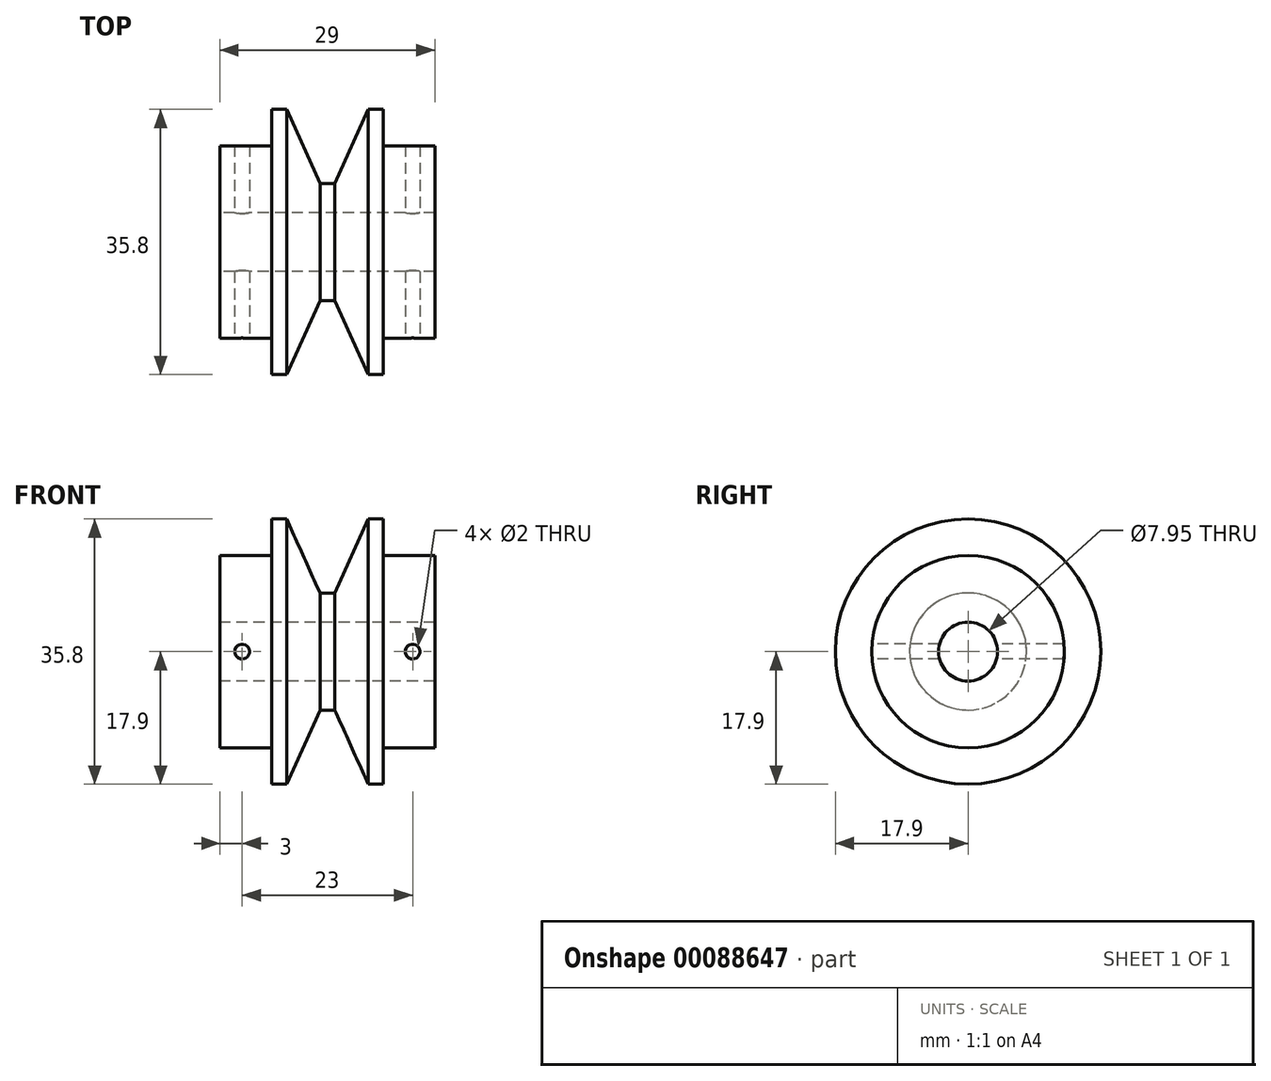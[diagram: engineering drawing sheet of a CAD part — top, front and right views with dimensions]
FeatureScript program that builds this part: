
annotation { "Feature Type Name" : "Feature", "Feature Type Description" : "" }
export const myFeature = defineFeature(function(context is Context, id is Id, definition is map)
    precondition{}
    {
        {
            var Q0;
            Q0=qCreatedBy(makeId("Right.planeOp"),FACE);
            var sketch = newSketch(context, id + "F0", { "sketchPlane" : qUnion([Q0])});
            skCircle(sketch, "E0", {"center": v(0, 0) * mm, "radius": 3.98 * mm});
            skCircle(sketch, "E1", {"center": v(0, 0) * mm, "radius": 13 * mm});
            skSolve(sketch);
        }
        {
            var Q0;
            Q0=makeQuery(id+"F0.imprint","IMPRINT",FACE,{"disambiguationData":[TD([[makeQuery(id+"F0.imprint","IMPRINT",EDGE,{"derivedFrom":sQuery(id+"F0.wireOp",EDGE,"E0")}),-1.0]])]});
            extrude(context, id + "F1", {"entities" : qUnion([Q0]), "endBound" : BoundingType.SYMMETRIC, "depth" : 29 * mm});
        }
        {
            var Q0;
            Q0=qCreatedBy(makeId("Front.planeOp"),FACE);
            var sketch = newSketch(context, id + "F2", { "sketchPlane" : qUnion([Q0])});
            skLineSegment(sketch, "E2", {"start": v(-27.37, 0) * mm, "end": v(29.66, 0) * mm});
            skLineSegment(sketch, "E3.bottom", {"start": v(-7.5, 17.9) * mm, "end": v(7.5, 17.9) * mm});
            skLineSegment(sketch, "E3.top", {"start": v(-7.5, 7.9) * mm, "end": v(7.5, 7.9) * mm});
            skLineSegment(sketch, "E3.left", {"start": v(-7.5, 17.9) * mm, "end": v(-7.5, 7.9) * mm});
            skLineSegment(sketch, "E3.right", {"start": v(7.5, 17.9) * mm, "end": v(7.5, 7.9) * mm});
            skLineSegment(sketch, "E4", {"start": v(-5.5, 17.9) * mm, "end": v(-1, 7.9) * mm});
            skLineSegment(sketch, "E5", {"start": v(5.5, 17.9) * mm, "end": v(1, 7.9) * mm});
            skSolve(sketch);
        }
        {
            var Q0;
            {var subQ0=sQuery(id+"F2.wireOp",EDGE,"E3.left");Q0=makeQuery(id+"F2.imprint","IMPRINT",FACE,{"disambiguationData":[TD([[makeQuery(id+"F2.imprint","IMPRINT",EDGE,{"derivedFrom":subQ0}),1.0]])]});}
            var Q1;
            {var subQ0=sQuery(id+"F2.wireOp",EDGE,"E3.right");Q1=makeQuery(id+"F2.imprint","IMPRINT",FACE,{"disambiguationData":[TD([[makeQuery(id+"F2.imprint","IMPRINT",EDGE,{"derivedFrom":subQ0}),-1.0]])]});}
            var Q2;
            Q2=sQuery(id+"F2.wireOp",EDGE,"E2");
            revolve(context, id + "F3", {"operationType" : NewBodyOperationType.ADD, "entities" : qUnion([Q0, Q1]), "axis" : qUnion([Q2]), "revolveType" : RevolveType.FULL});
        }
        {
            var Q0;
            Q0=qCreatedBy(makeId("Front.planeOp"),FACE);
            var sketch = newSketch(context, id + "F4", { "sketchPlane" : qUnion([Q0])});
            skCircle(sketch, "E6", {"center": v(-11.5, 0) * mm, "radius": 1 * mm});
            skCircle(sketch, "E7", {"center": v(11.5, 0) * mm, "radius": 1 * mm});
            skSolve(sketch);
        }
        {
            var Q0;
            Q0=makeQuery(id+"F4.imprint","IMPRINT",FACE,{"disambiguationData":[TD([[makeQuery(id+"F4.imprint","IMPRINT",EDGE,{"derivedFrom":sQuery(id+"F4.wireOp",EDGE,"E6")}),1.0]])]});
            var Q1;
            Q1=makeQuery(id+"F4.imprint","IMPRINT",FACE,{"disambiguationData":[TD([[makeQuery(id+"F4.imprint","IMPRINT",EDGE,{"derivedFrom":sQuery(id+"F4.wireOp",EDGE,"E7")}),1.0]])]});
            extrude(context, id + "F5", {"entities" : qUnion([Q0, Q1]), "operationType" : NewBodyOperationType.REMOVE, "endBound" : BoundingType.SYMMETRIC, "oppositeDirection" : true, "depth" : 30 * mm});
        }
        {
            var Q0;
            {var subQ0=sQuery(id+"F2.wireOp",EDGE,"E4");Q0=makeQuery(id+"F2.imprint","IMPRINT",FACE,{"disambiguationData":[TD([[makeQuery(id+"F2.imprint","IMPRINT",EDGE,{"derivedFrom":subQ0}),1.0]])]});}
            var Q1;
            Q1=sQuery(id+"F2.wireOp",EDGE,"E2");
            revolve(context, id + "F6", {"operationType" : NewBodyOperationType.REMOVE, "entities" : qUnion([Q0]), "axis" : qUnion([Q1]), "revolveType" : RevolveType.FULL, "oppositeDirection" : true});
        }
    });
